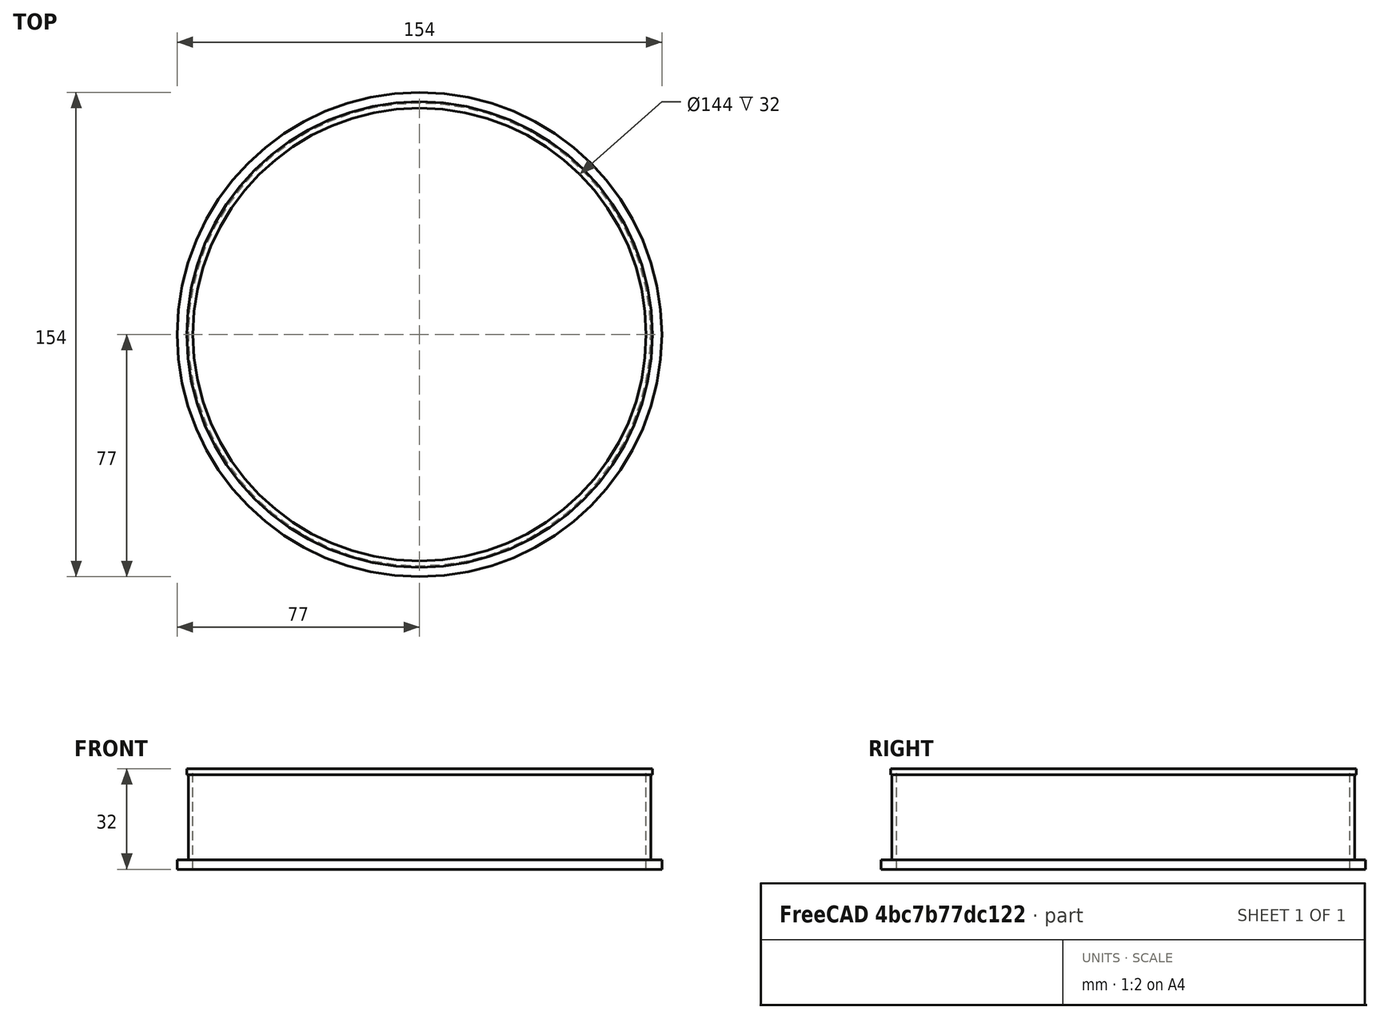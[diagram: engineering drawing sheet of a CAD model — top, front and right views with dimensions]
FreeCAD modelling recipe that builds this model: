
FCSTD DOCUMENT  (FreeCAD 0.21R33771 (Git))
Label: Переходник для филтра 2
License: All rights reserved
LicenseURL: http://en.wikipedia.org/wiki/All_rights_reserved
objects: Part::FeaturePython×3, Part::MultiFuse×1
note: 4 computed .brp shape members not serialized (recipe doc carries the construction recipe); baked Part::Feature solids carry a one-line shape summary decoded from their .brp

FEATURE [Part::FeaturePython] Tube  # WARN: FeaturePython — macro-defined, semantics opaque (R4)
  AttacherType = Attacher::AttachEngine3D
  Height = 3
  InnerRadius = 72
  OuterRadius = 77
FEATURE [Part::FeaturePython] Tube001  # WARN: FeaturePython — macro-defined, semantics opaque (R4)
  AttacherType = Attacher::AttachEngine3D
  Height = 30
  InnerRadius = 72
  OuterRadius = 73.5
FEATURE [Part::FeaturePython] Tube002  # WARN: FeaturePython — macro-defined, semantics opaque (R4)
  AttacherType = Attacher::AttachEngine3D
  Height = 2
  InnerRadius = 72
  OuterRadius = 74
  Placement = pos=(0,0,30) rot=(0,0,1;0rad)
FEATURE [Part::MultiFuse] Fusion
  Refine = true
  Shapes = -> [Tube002,Tube001,Tube]
